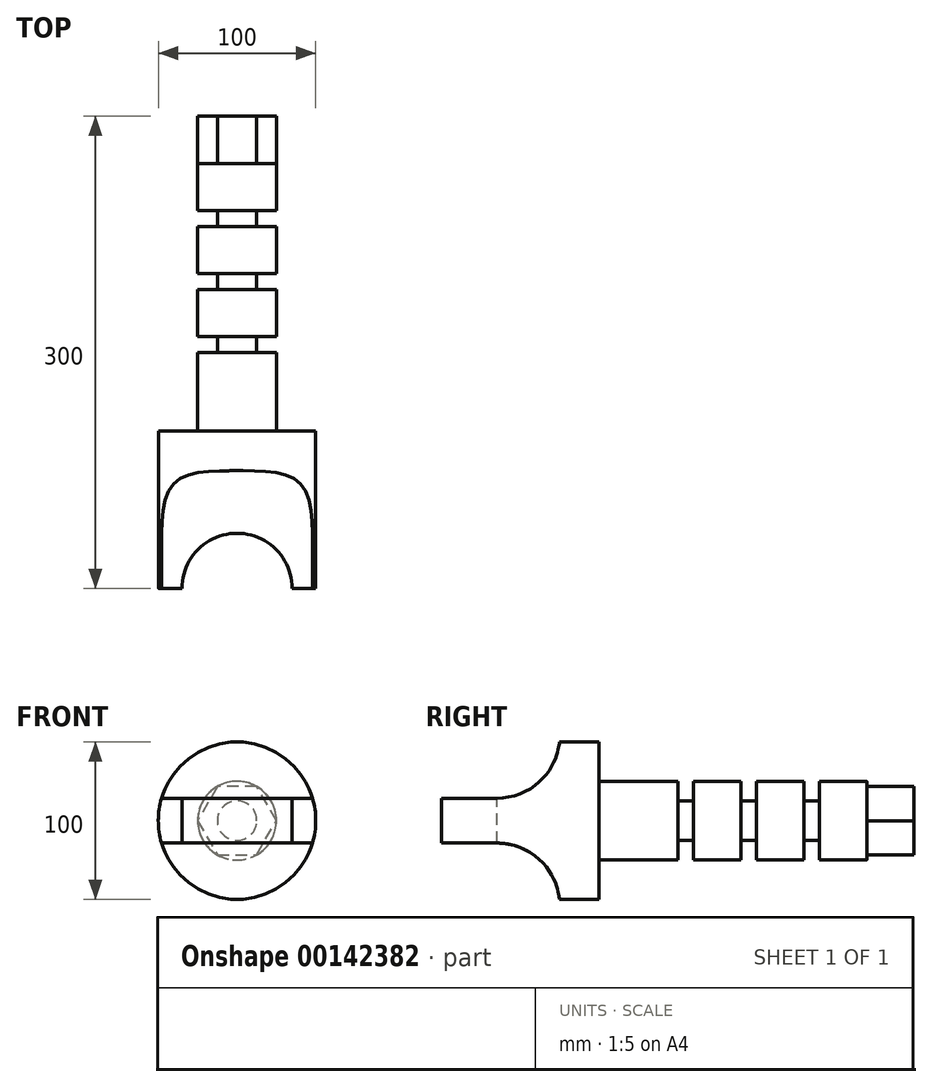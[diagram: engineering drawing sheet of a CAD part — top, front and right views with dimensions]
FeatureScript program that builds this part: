
annotation { "Feature Type Name" : "Feature", "Feature Type Description" : "" }
export const myFeature = defineFeature(function(context is Context, id is Id, definition is map)
    precondition{}
    {
        {
            var Q0;
            Q0=qCreatedBy(makeId("Front.planeOp"),FACE);
            var sketch = newSketch(context, id + "F0", { "sketchPlane" : qUnion([Q0])});
            skCircle(sketch, "E0", {"center": v(0, 0) * mm, "radius": 50 * mm});
            skSolve(sketch);
        }
        {
            var Q0;
            Q0=makeQuery(id+"F0.imprint","IMPRINT",FACE,{"disambiguationData":[TD([[makeQuery(id+"F0.imprint","IMPRINT",EDGE,{"derivedFrom":sQuery(id+"F0.wireOp",EDGE,"E0")}),1.0]])]});
            extrude(context, id + "F1", {"entities" : qUnion([Q0]), "depth" : 100 * mm});
        }
        {
            var Q0;
            Q0=makeQuery(id+"F1.opExtrude","CAP_FACE",FACE,{"disambiguationData":[OSD([sQuery(id+"F0.wireOp",EDGE,"E0")])],"isStart":true});
            var sketch = newSketch(context, id + "F2", { "sketchPlane" : qUnion([Q0])});
            skCircle(sketch, "E1", {"center": v(0, 0) * mm, "radius": 25 * mm});
            skSolve(sketch);
        }
        {
            var Q0;
            Q0 = qSketchRegion(id + "F2", true);
            extrude(context, id + "F3", {"entities" : qUnion([Q0]), "operationType" : NewBodyOperationType.ADD, "depth" : 50 * mm});
        }
        {
            var Q0;
            Q0=makeQuery(id+"F3.opExtrude","CAP_FACE",FACE,{"disambiguationData":[OSD([sQuery(id+"F2.wireOp",EDGE,"E1")])],"isStart":false});
            var sketch = newSketch(context, id + "F4", { "sketchPlane" : qUnion([Q0])});
            skCircle(sketch, "E2", {"center": v(0, 0) * mm, "radius": 12.5 * mm});
            skSolve(sketch);
        }
        {
            var Q0;
            Q0 = qSketchRegion(id + "F4", true);
            extrude(context, id + "F5", {"entities" : qUnion([Q0]), "operationType" : NewBodyOperationType.ADD, "depth" : 10 * mm});
        }
        {
            var Q0;
            Q0=makeQuery(id+"F5.opExtrude","CAP_FACE",FACE,{"disambiguationData":[OSD([sQuery(id+"F4.wireOp",EDGE,"E2")])],"isStart":false});
            var sketch = newSketch(context, id + "F6", { "sketchPlane" : qUnion([Q0])});
            skCircle(sketch, "E3", {"center": v(0, 0) * mm, "radius": 25 * mm});
            skSolve(sketch);
        }
        {
            var Q0;
            Q0 = qSketchRegion(id + "F6", true);
            extrude(context, id + "F7", {"entities" : qUnion([Q0]), "operationType" : NewBodyOperationType.ADD, "depth" : 30 * mm});
        }
        {
            var Q0;
            Q0=makeQuery(id+"F7.opExtrude","CAP_FACE",FACE,{"disambiguationData":[OSD([sQuery(id+"F6.wireOp",EDGE,"E3")])],"isStart":false});
            var sketch = newSketch(context, id + "F8", { "sketchPlane" : qUnion([Q0])});
            skCircle(sketch, "E4", {"center": v(0, 0) * mm, "radius": 12.5 * mm});
            skSolve(sketch);
        }
        {
            var Q0;
            Q0 = qSketchRegion(id + "F8", true);
            extrude(context, id + "F9", {"entities" : qUnion([Q0]), "operationType" : NewBodyOperationType.ADD, "depth" : 10 * mm});
        }
        {
            var Q0;
            Q0=makeQuery(id+"F9.opExtrude","CAP_FACE",FACE,{"disambiguationData":[OSD([sQuery(id+"F8.wireOp",EDGE,"E4")])],"isStart":false});
            var sketch = newSketch(context, id + "F10", { "sketchPlane" : qUnion([Q0])});
            skCircle(sketch, "E5", {"center": v(0, 0) * mm, "radius": 25 * mm});
            skSolve(sketch);
        }
        {
            var Q0;
            Q0 = qSketchRegion(id + "F10", true);
            extrude(context, id + "F11", {"entities" : qUnion([Q0]), "operationType" : NewBodyOperationType.ADD, "depth" : 30 * mm});
        }
        {
            var Q0;
            Q0=makeQuery(id+"F11.opExtrude","CAP_FACE",FACE,{"disambiguationData":[OSD([sQuery(id+"F10.wireOp",EDGE,"E5")])],"isStart":false});
            var sketch = newSketch(context, id + "F12", { "sketchPlane" : qUnion([Q0])});
            skCircle(sketch, "E6", {"center": v(0, 0) * mm, "radius": 12.5 * mm});
            skSolve(sketch);
        }
        {
            var Q0;
            Q0 = qSketchRegion(id + "F12", true);
            extrude(context, id + "F13", {"entities" : qUnion([Q0]), "operationType" : NewBodyOperationType.ADD, "depth" : 10 * mm});
        }
        {
            var Q0;
            Q0=makeQuery(id+"F13.opExtrude","CAP_FACE",FACE,{"disambiguationData":[OSD([sQuery(id+"F12.wireOp",EDGE,"E6")])],"isStart":false});
            var sketch = newSketch(context, id + "F14", { "sketchPlane" : qUnion([Q0])});
            skCircle(sketch, "E7", {"center": v(0, 0) * mm, "radius": 25 * mm});
            skSolve(sketch);
        }
        {
            var Q0;
            Q0 = qSketchRegion(id + "F14", true);
            extrude(context, id + "F15", {"entities" : qUnion([Q0]), "operationType" : NewBodyOperationType.ADD, "depth" : 30 * mm});
        }
        {
            var Q0;
            Q0=makeQuery(id+"F15.opExtrude","CAP_FACE",FACE,{"disambiguationData":[OSD([sQuery(id+"F14.wireOp",EDGE,"E7")])],"isStart":false});
            var sketch = newSketch(context, id + "F16", { "sketchPlane" : qUnion([Q0])});
            skCircle(sketch, "E8.cCircle", {"center": v(0, 0) * mm, "radius": 25 * mm, "construction": true});
            skLineSegment(sketch, "E8.0", {"start": v(25, 0) * mm, "end": v(12.5, -21.65) * mm});
            skLineSegment(sketch, "E8.1", {"start": v(12.5, -21.65) * mm, "end": v(-12.5, -21.65) * mm});
            skLineSegment(sketch, "E8.2", {"start": v(-12.5, -21.65) * mm, "end": v(-25, 0) * mm});
            skLineSegment(sketch, "E8.3", {"start": v(-25, 0) * mm, "end": v(-12.5, 21.65) * mm});
            skLineSegment(sketch, "E8.4", {"start": v(-12.5, 21.65) * mm, "end": v(12.5, 21.65) * mm});
            skLineSegment(sketch, "E8.5", {"start": v(12.5, 21.65) * mm, "end": v(25, 0) * mm});
            skSolve(sketch);
        }
        {
            var Q0;
            Q0 = qSketchRegion(id + "F16", true);
            extrude(context, id + "F17", {"entities" : qUnion([Q0]), "operationType" : NewBodyOperationType.ADD, "depth" : 30 * mm});
        }
        {
            var Q0;
            Q0=qCreatedBy(makeId("Top.planeOp"),FACE);
            cPlane(context, id + "F18", {"entities" : qUnion([Q0]), "cplaneType" : CPlaneType.OFFSET, "offset" : 50 * mm, "width" : 150 * mm, "height" : 150 * mm});
        }
        {
            var Q0;
            Q0=qCreatedBy(id+"F18.planeOp",FACE);
            var sketch = newSketch(context, id + "F19", { "sketchPlane" : qUnion([Q0])});
            skCircle(sketch, "E9", {"center": v(0, -99.94) * mm, "radius": 35 * mm});
            skSolve(sketch);
        }
        {
            var Q0;
            Q0=sQuery(id+"F19.wireOp",VERTEX,"E9.center");
            var Q1;
            Q1=makeQuery(id+"F1.opExtrude","SWEPT_BODY",BODY,{"disambiguationData":[OSD([sQuery(id+"F0.wireOp",EDGE,"E0")])]});
            hole(context, id + "F20", {"style" : HoleStyle.SIMPLE, "endStyle" : HoleEndStyle.THROUGH, "holeDiameter" : 70 * mm, "locations" : qUnion([Q0]), "scope" : qUnion([Q1]), "isTappedThrough" : true});
        }
        {
            var Q0;
            Q0=makeQuery(id+"F20.hole-0.boolean.opBoolean","SPLIT",FACE,{"disambiguationData":[OD(0.0)],"derivedFrom":makeQuery(id+"F1.opExtrude","CAP_FACE",FACE,{"disambiguationData":[OSD([sQuery(id+"F0.wireOp",EDGE,"E0")])],"isStart":false})});
            var sketch = newSketch(context, id + "F21", { "sketchPlane" : qUnion([Q0])});
            skLineSegment(sketch, "E10", {"start": v(-47.93, 14.25) * mm, "end": v(48.43, 14.25) * mm});
            skArc(sketch, "E11", {"start": v(-47.93, 14.25) * mm, "mid": v(0, 50) * mm, "end": v(47.93, 14.25) * mm});
            skLineSegment(sketch, "E12", {"start": v(-47.93, -14.25) * mm, "end": v(48.8, -14.25) * mm});
            skArc(sketch, "E13", {"start": v(-47.93, -14.25) * mm, "mid": v(0, -50) * mm, "end": v(47.93, -14.25) * mm});
            skSolve(sketch);
        }
        {
            var Q0;
            Q0 = qSketchRegion(id + "F21", true);
            extrude(context, id + "F22", {"entities" : qUnion([Q0]), "operationType" : NewBodyOperationType.REMOVE, "oppositeDirection" : true, "depth" : 75 * mm});
        }
        {
            var Q0;
            Q0=makeQuery(id+"F22.boolean.opBoolean","COPY",EDGE,{"derivedFrom":makeQuery(id+"F22.opExtrude","CAP_EDGE",EDGE,{"disambiguationData":[OSD([sQuery(id+"F21.wireOp",EDGE,"E10")])],"isStart":false})});
            var Q1;
            Q1=makeQuery(id+"F22.boolean.opBoolean","COPY",EDGE,{"derivedFrom":makeQuery(id+"F22.opExtrude","CAP_EDGE",EDGE,{"disambiguationData":[OSD([sQuery(id+"F21.wireOp",EDGE,"E12")])],"isStart":false})});
            fillet(context, id + "F23", {"entities" : qUnion([Q0, Q1]), "radius" : 39.9 * mm, "tangentPropagation" : true, "allowEdgeOverflow" : false});
        }
    });
